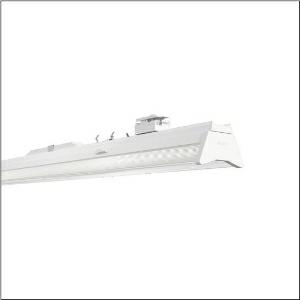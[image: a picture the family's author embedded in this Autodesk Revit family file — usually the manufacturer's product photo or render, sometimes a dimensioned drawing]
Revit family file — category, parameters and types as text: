
# Revit family: licross_r__21_performance_mo_52td16vn48xg_2cf7
name_source: partatom
category: Lighting Fixtures
units: mm (PartAtom-declared; Revit-internal decimal feet)

## family parameters
Cut with Voids When Loaded = No
Host = Face
Light Source = No
Part Type = Normal
Room Calculation Point = No
Round Connector Dimension = Use Diameter
Shared = No

## types (1)
- --- (1 x LED, 8000 lm, 44.6 W, 4000K)
    Apparent Load = 45 VA
    CIE Flux Codes = 66 88 96 79 100
    Color Rendering = 80
    Color Temperature = 4000K
    Default Elevation = 1800 mm
    Description = Licross® 21 Performance MO, luminaire insert, of sheet steel, galvanised, coil coated, white, length: 1.500mm, width: 120mm, height: 123mm, LED rated luminous flux: 8.000lm, light colour: 840, control gear: DALI 2, CLO, with plug, 5-pole, with phase selection, mains connection: 220..240V, AC, 50/60Hz, start of lifetime: 45W, end of service life: 53W, halogen-free wiring, primary light control with lens, of plastic, primary optical cover: cover, of PMMA, light emission: direct/indirect distribution, primary light characteristic: symmetric, protection rating (complete): IP54, insulation class (complete): insulation class I (protective earthing), certification: CE, ENEC, VDE, UKCA, protection symbol: D if used in an environment with non-conductive dust loads with corresponding accessories, impact resistance: IK06, permissible ambient temperature for indoor applications: -25..+45°C, corresponds to IFS (International Featured Standards) requirements for safety and quality in the food industry, reducing of maximum allowable ambient temperature of 5°C with ceiling mounting, LABS conformity tested according to VDMA 24364:2018-05, packaging unit: 1 piece
    Height = 114 mm
    Lamp = 1 x LED
    Lamp Light Flux = 8000 lm
    Lamp Power = 44.6 W
    Lamp count = 1
    Length = 1500 mm
    Luminous efficacy = 179 lm/W
    Manufacturer = Siteco
    ModVariant = No
    Model = 52TD16VN48XG
    Mounting Place = Ceiling
    Mounting Type = Pendant
    Number of Poles = 1
    OnlyDefault = Yes
    Power Factor = 1
    Product Name = Licross® 21 Performance MO
    Product group = luminaire insert
    ProductGroupID = 902
    Protection Class = Protection class I
    Protection Degree = IP 54
    RLX_Detail_Level = 1
    RLX_Emergency_Light_Flux = 0 lm
    RLX_Emergency_Type = 0
    RLX_Emergency_Type_DB = No
    RlxData = <blob elided: 34021 chars, md5=f470d9fa>
    Socket = socket
    Standby Power = 0 W
    System Light Flux = 8000 lm
    System Power = 45 W
    Type Comments = factory setting: luminous flux: 100 % | dim-lin: 254 | 301 mA
    Type Image = l_1256138.jpg
    URL = http://relux.com
    VarID = @adj_083026
    Voltage = 0 V
    Weight = 0.00 kg
    Width = 120 mm

## geometry (parser evidence)
native form markers: Blend x4, Sweep x12
no freeform markers — native parametric forms only
